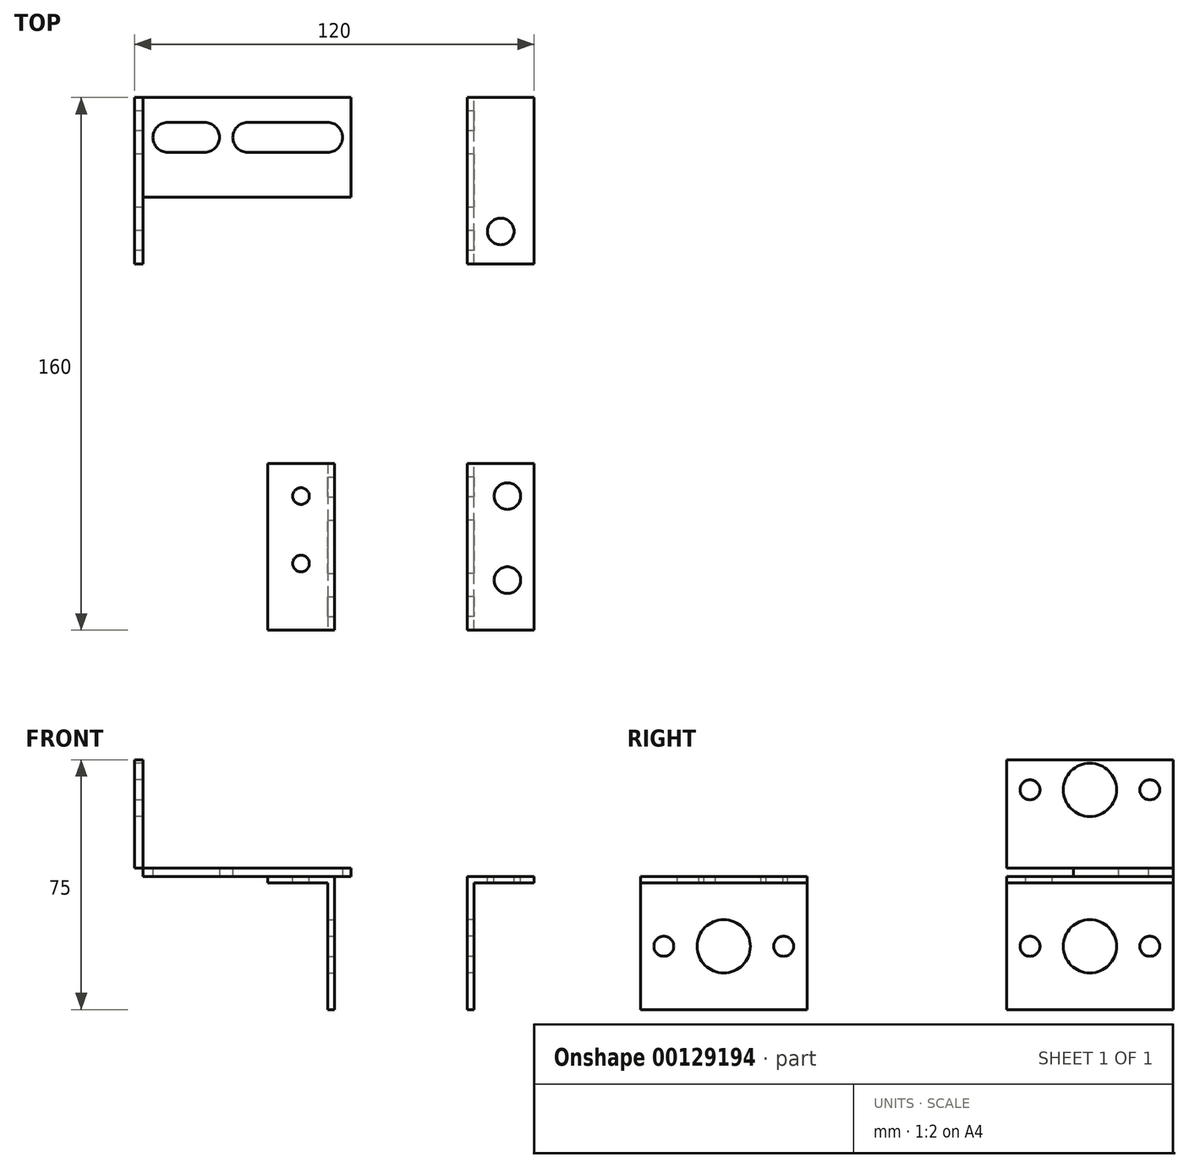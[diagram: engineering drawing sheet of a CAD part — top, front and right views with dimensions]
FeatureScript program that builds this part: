
annotation { "Feature Type Name" : "Feature", "Feature Type Description" : "" }
export const myFeature = defineFeature(function(context is Context, id is Id, definition is map)
    precondition{}
    {
        {
            var Q0;
            Q0=qCreatedBy(makeId("Front.planeOp"),FACE);
            cPlane(context, id + "F0", {"entities" : qUnion([Q0]), "cplaneType" : CPlaneType.OFFSET, "offset" : 80 * mm, "width" : 150 * mm, "height" : 150 * mm});
        }
        {
            var Q0;
            Q0=qCreatedBy(makeId("Front.planeOp"),FACE);
            cPlane(context, id + "F1", {"entities" : qUnion([Q0]), "cplaneType" : CPlaneType.OFFSET, "offset" : 80 * mm, "oppositeDirection" : true, "width" : 150 * mm, "height" : 150 * mm});
        }
        {
            var Q0;
            Q0=qCreatedBy(id+"F0.planeOp",FACE);
            var sketch = newSketch(context, id + "F2", { "sketchPlane" : qUnion([Q0])});
            skLineSegment(sketch, "E0.bottom", {"start": v(-20, 0) * mm, "end": v(-40, 0) * mm});
            skLineSegment(sketch, "E0.top", {"start": v(-20, -2) * mm, "end": v(-40, -2) * mm});
            skLineSegment(sketch, "E0.left", {"start": v(-20, 0) * mm, "end": v(-20, -2) * mm});
            skLineSegment(sketch, "E0.right", {"start": v(-40, 0) * mm, "end": v(-40, -2) * mm});
            skLineSegment(sketch, "E1.bottom", {"start": v(-20, 0) * mm, "end": v(-22, 0) * mm});
            skLineSegment(sketch, "E1.top", {"start": v(-20, -40) * mm, "end": v(-22, -40) * mm});
            skLineSegment(sketch, "E1.left", {"start": v(-20, 0) * mm, "end": v(-20, -40) * mm});
            skLineSegment(sketch, "E1.right", {"start": v(-22, 0) * mm, "end": v(-22, -40) * mm});
            skSolve(sketch);
        }
        {
            var Q0;
            {var subQ0=sQuery(id+"F2.wireOp",EDGE,"E0.bottom");Q0=makeQuery(id+"F2.imprint","IMPRINT",FACE,{"disambiguationData":[TD([[makeQuery(id+"F2.imprint","IMPRINT",EDGE,{"derivedFrom":subQ0}),1.0]])]});}
            var Q1;
            {var subQ5=sQuery(id+"F2.wireOp",EDGE,"E1.bottom");Q1=makeQuery(id+"F2.imprint","IMPRINT",FACE,{"disambiguationData":[TD([[makeQuery(id+"F2.imprint","IMPRINT",EDGE,{"derivedFrom":subQ5}),1.0]])]});}
            extrude(context, id + "F3", {"entities" : qUnion([Q0, Q1]), "oppositeDirection" : true, "depth" : 50 * mm});
        }
        {
            var Q0;
            {var subQ5=sQuery(id+"F2.wireOp",EDGE,"E1.top");Q0=makeQuery(id+"F2.imprint","IMPRINT",FACE,{"disambiguationData":[TD([[makeQuery(id+"F2.imprint","IMPRINT",EDGE,{"derivedFrom":subQ5}),-1.0]])]});}
            var Q1;
            {var subQ5=sQuery(id+"F2.wireOp",EDGE,"E1.bottom");Q1=makeQuery(id+"F2.imprint","IMPRINT",FACE,{"disambiguationData":[TD([[makeQuery(id+"F2.imprint","IMPRINT",EDGE,{"derivedFrom":subQ5}),1.0]])]});}
            extrude(context, id + "F4", {"entities" : qUnion([Q0, Q1]), "operationType" : NewBodyOperationType.ADD, "oppositeDirection" : true, "depth" : 50 * mm});
        }
        {
            var Q0;
            {var subQ0=sQuery(id+"F2.wireOp",EDGE,"E1.left");Q0=makeQuery(id+"F4.boolean.opBoolean","MERGE",FACE,{"derivedFrom":[makeQuery(id+"F3.opExtrude","SWEPT_FACE",FACE,{"disambiguationData":[OSD([subQ0])]}),makeQuery(id+"F4.opExtrude","SWEPT_FACE",FACE,{"disambiguationData":[OSD([subQ0])]})]});}
            var sketch = newSketch(context, id + "F5", { "sketchPlane" : qUnion([Q0])});
            skCircle(sketch, "E2", {"center": v(-55, -21) * mm, "radius": 8 * mm});
            skCircle(sketch, "E3", {"center": v(-73, -21) * mm, "radius": 3 * mm});
            skCircle(sketch, "E4", {"center": v(-37, -21) * mm, "radius": 3 * mm});
            skLineSegment(sketch, "E5", {"start": v(-73, -21) * mm, "end": v(-55, -21) * mm, "construction": true});
            skLineSegment(sketch, "E6", {"start": v(-55, -21) * mm, "end": v(-37, -21) * mm, "construction": true});
            skSolve(sketch);
        }
        {
            var Q0;
            Q0=makeQuery(id+"F3.opExtrude","SWEPT_FACE",FACE,{"disambiguationData":[OSD([sQuery(id+"F2.wireOp",EDGE,"E0.bottom"),sQuery(id+"F2.wireOp",EDGE,"E1.bottom")])]});
            var sketch = newSketch(context, id + "F6", { "sketchPlane" : qUnion([Q0])});
            skCircle(sketch, "E7", {"center": v(-30, -39.75) * mm, "radius": 2.5 * mm});
            skCircle(sketch, "E8", {"center": v(-30, -60) * mm, "radius": 2.5 * mm});
            skSolve(sketch);
        }
        {
            var Q0;
            Q0=makeQuery(id+"F5.imprint","IMPRINT",FACE,{"disambiguationData":[TD([[makeQuery(id+"F5.imprint","IMPRINT",EDGE,{"derivedFrom":sQuery(id+"F5.wireOp",EDGE,"E3")}),1.0]])]});
            var Q1;
            Q1=makeQuery(id+"F5.imprint","IMPRINT",FACE,{"disambiguationData":[TD([[makeQuery(id+"F5.imprint","IMPRINT",EDGE,{"derivedFrom":sQuery(id+"F5.wireOp",EDGE,"E2")}),1.0]])]});
            var Q2;
            Q2=makeQuery(id+"F5.imprint","IMPRINT",FACE,{"disambiguationData":[TD([[makeQuery(id+"F5.imprint","IMPRINT",EDGE,{"derivedFrom":sQuery(id+"F5.wireOp",EDGE,"E4")}),1.0]])]});
            extrude(context, id + "F7", {"entities" : qUnion([Q0, Q1, Q2]), "operationType" : NewBodyOperationType.REMOVE, "endBound" : BoundingType.SYMMETRIC, "oppositeDirection" : true, "depth" : 10 * mm});
        }
        {
            var Q0;
            Q0=makeQuery(id+"F6.imprint","IMPRINT",FACE,{"disambiguationData":[TD([[makeQuery(id+"F6.imprint","IMPRINT",EDGE,{"derivedFrom":sQuery(id+"F6.wireOp",EDGE,"E7")}),1.0]])]});
            var Q1;
            Q1=makeQuery(id+"F6.imprint","IMPRINT",FACE,{"disambiguationData":[TD([[makeQuery(id+"F6.imprint","IMPRINT",EDGE,{"derivedFrom":sQuery(id+"F6.wireOp",EDGE,"E8")}),1.0]])]});
            extrude(context, id + "F8", {"entities" : qUnion([Q0, Q1]), "operationType" : NewBodyOperationType.REMOVE, "endBound" : BoundingType.SYMMETRIC, "oppositeDirection" : true, "depth" : 10 * mm});
        }
        {
            var Q0;
            Q0=qCreatedBy(id+"F0.planeOp",FACE);
            var sketch = newSketch(context, id + "F9", { "sketchPlane" : qUnion([Q0])});
            skLineSegment(sketch, "E9.top", {"start": v(20, -2) * mm, "end": v(40, -2) * mm});
            skLineSegment(sketch, "E9.left", {"start": v(20, 0) * mm, "end": v(20, -2) * mm});
            skLineSegment(sketch, "E9.right", {"start": v(40, 0) * mm, "end": v(40, -2) * mm});
            skLineSegment(sketch, "E10.bottom", {"start": v(20, 0) * mm, "end": v(22, 0) * mm});
            skLineSegment(sketch, "E10.top", {"start": v(20, -40) * mm, "end": v(22, -40) * mm});
            skLineSegment(sketch, "E10.left", {"start": v(20, 0) * mm, "end": v(20, -40) * mm});
            skLineSegment(sketch, "E10.right", {"start": v(22, 0) * mm, "end": v(22, -40) * mm});
            skLineSegment(sketch, "E11", {"start": v(22, 0) * mm, "end": v(40, 0) * mm});
            skSolve(sketch);
        }
        {
            var Q0;
            {var subQ0=sQuery(id+"F9.wireOp",EDGE,"E9.right");Q0=makeQuery(id+"F9.imprint","IMPRINT",FACE,{"disambiguationData":[TD([[makeQuery(id+"F9.imprint","IMPRINT",EDGE,{"derivedFrom":subQ0}),-1.0]])]});}
            var Q1;
            {var subQ5=sQuery(id+"F9.wireOp",EDGE,"E10.bottom");Q1=makeQuery(id+"F9.imprint","IMPRINT",FACE,{"disambiguationData":[TD([[makeQuery(id+"F9.imprint","IMPRINT",EDGE,{"derivedFrom":subQ5}),-1.0]])]});}
            extrude(context, id + "F10", {"entities" : qUnion([Q0, Q1]), "oppositeDirection" : true, "depth" : 50 * mm});
        }
        {
            var Q0;
            {var subQ5=sQuery(id+"F9.wireOp",EDGE,"E10.bottom");Q0=makeQuery(id+"F9.imprint","IMPRINT",FACE,{"disambiguationData":[TD([[makeQuery(id+"F9.imprint","IMPRINT",EDGE,{"derivedFrom":subQ5}),-1.0]])]});}
            var Q1;
            {var subQ5=sQuery(id+"F9.wireOp",EDGE,"E10.top");Q1=makeQuery(id+"F9.imprint","IMPRINT",FACE,{"disambiguationData":[TD([[makeQuery(id+"F9.imprint","IMPRINT",EDGE,{"derivedFrom":subQ5}),1.0]])]});}
            extrude(context, id + "F11", {"entities" : qUnion([Q0, Q1]), "operationType" : NewBodyOperationType.ADD, "oppositeDirection" : true, "depth" : 50 * mm});
        }
        {
            var Q0;
            {var subQ0=sQuery(id+"F9.wireOp",EDGE,"E10.left");Q0=makeQuery(id+"F11.boolean.opBoolean","MERGE",FACE,{"derivedFrom":[makeQuery(id+"F10.opExtrude","SWEPT_FACE",FACE,{"disambiguationData":[OSD([subQ0])]}),makeQuery(id+"F11.opExtrude","SWEPT_FACE",FACE,{"disambiguationData":[OSD([subQ0])]})]});}
            var sketch = newSketch(context, id + "F12", { "sketchPlane" : qUnion([Q0])});
            skCircle(sketch, "E12", {"center": v(55, -21) * mm, "radius": 8 * mm});
            skCircle(sketch, "E13", {"center": v(37, -21) * mm, "radius": 3 * mm});
            skCircle(sketch, "E14", {"center": v(73, -21) * mm, "radius": 3 * mm});
            skLineSegment(sketch, "E15", {"start": v(37, -21) * mm, "end": v(55, -21) * mm, "construction": true});
            skLineSegment(sketch, "E16", {"start": v(55, -21) * mm, "end": v(73, -21) * mm, "construction": true});
            skSolve(sketch);
        }
        {
            var Q0;
            Q0=makeQuery(id+"F10.opExtrude","SWEPT_FACE",FACE,{"disambiguationData":[OSD([sQuery(id+"F9.wireOp",EDGE,"E10.bottom"),sQuery(id+"F9.wireOp",EDGE,"E11")])]});
            var sketch = newSketch(context, id + "F13", { "sketchPlane" : qUnion([Q0])});
            skCircle(sketch, "E17", {"center": v(32, -65) * mm, "radius": 4 * mm});
            skCircle(sketch, "E18", {"center": v(32, -39.75) * mm, "radius": 4 * mm});
            skSolve(sketch);
        }
        {
            var Q0;
            Q0=makeQuery(id+"F12.imprint","IMPRINT",FACE,{"disambiguationData":[TD([[makeQuery(id+"F12.imprint","IMPRINT",EDGE,{"derivedFrom":sQuery(id+"F12.wireOp",EDGE,"E13")}),1.0]])]});
            var Q1;
            Q1=makeQuery(id+"F12.imprint","IMPRINT",FACE,{"disambiguationData":[TD([[makeQuery(id+"F12.imprint","IMPRINT",EDGE,{"derivedFrom":sQuery(id+"F12.wireOp",EDGE,"E12")}),1.0]])]});
            var Q2;
            Q2=makeQuery(id+"F12.imprint","IMPRINT",FACE,{"disambiguationData":[TD([[makeQuery(id+"F12.imprint","IMPRINT",EDGE,{"derivedFrom":sQuery(id+"F12.wireOp",EDGE,"E14")}),1.0]])]});
            extrude(context, id + "F14", {"entities" : qUnion([Q0, Q1, Q2]), "operationType" : NewBodyOperationType.REMOVE, "endBound" : BoundingType.SYMMETRIC, "oppositeDirection" : true, "depth" : 10 * mm});
        }
        {
            var Q0;
            Q0=makeQuery(id+"F13.imprint","IMPRINT",FACE,{"disambiguationData":[TD([[makeQuery(id+"F13.imprint","IMPRINT",EDGE,{"derivedFrom":sQuery(id+"F13.wireOp",EDGE,"E17")}),1.0]])]});
            var Q1;
            Q1=makeQuery(id+"F13.imprint","IMPRINT",FACE,{"disambiguationData":[TD([[makeQuery(id+"F13.imprint","IMPRINT",EDGE,{"derivedFrom":sQuery(id+"F13.wireOp",EDGE,"E18")}),1.0]])]});
            extrude(context, id + "F15", {"entities" : qUnion([Q0, Q1]), "operationType" : NewBodyOperationType.REMOVE, "endBound" : BoundingType.SYMMETRIC, "oppositeDirection" : true, "depth" : 10 * mm});
        }
        {
            var Q0;
            Q0=qCreatedBy(id+"F1.planeOp",FACE);
            var sketch = newSketch(context, id + "F16", { "sketchPlane" : qUnion([Q0])});
            skLineSegment(sketch, "E19", {"start": v(-80, 57.72) * mm, "end": v(-80, -28.34) * mm, "construction": true});
            skLineSegment(sketch, "E20.bottom", {"start": v(-80, 0) * mm, "end": v(-77.5, 0) * mm});
            skLineSegment(sketch, "E20.top", {"start": v(-80, 35) * mm, "end": v(-77.5, 35) * mm});
            skLineSegment(sketch, "E20.left", {"start": v(-80, 0) * mm, "end": v(-80, 35) * mm});
            skLineSegment(sketch, "E20.right", {"start": v(-77.5, 0) * mm, "end": v(-77.5, 35) * mm});
            skLineSegment(sketch, "E21.bottom", {"start": v(-80, 0) * mm, "end": v(-15, 0) * mm});
            skLineSegment(sketch, "E21.top", {"start": v(-80, 2.5) * mm, "end": v(-15, 2.5) * mm});
            skLineSegment(sketch, "E21.left", {"start": v(-80, 0) * mm, "end": v(-80, 2.5) * mm});
            skLineSegment(sketch, "E21.right", {"start": v(-15, 0) * mm, "end": v(-15, 2.5) * mm});
            skSolve(sketch);
        }
        {
            var Q0;
            {var subQ5=sQuery(id+"F16.wireOp",EDGE,"E21.right");Q0=makeQuery(id+"F16.imprint","IMPRINT",FACE,{"disambiguationData":[TD([[makeQuery(id+"F16.imprint","IMPRINT",EDGE,{"derivedFrom":subQ5}),1.0]])]});}
            var Q1;
            {var subQ5=sQuery(id+"F16.wireOp",EDGE,"E21.left");Q1=makeQuery(id+"F16.imprint","IMPRINT",FACE,{"disambiguationData":[TD([[makeQuery(id+"F16.imprint","IMPRINT",EDGE,{"derivedFrom":subQ5}),-1.0]])]});}
            extrude(context, id + "F17", {"entities" : qUnion([Q0, Q1]), "depth" : 30 * mm});
        }
        {
            var Q0;
            {var subQ0=sQuery(id+"F16.wireOp",EDGE,"E20.top");Q0=makeQuery(id+"F16.imprint","IMPRINT",FACE,{"disambiguationData":[TD([[makeQuery(id+"F16.imprint","IMPRINT",EDGE,{"derivedFrom":subQ0}),-1.0]])]});}
            extrude(context, id + "F18", {"entities" : qUnion([Q0]), "operationType" : NewBodyOperationType.ADD, "depth" : 50 * mm});
        }
        {
            var Q0;
            Q0=makeQuery(id+"F18.boolean.opBoolean","MERGE",FACE,{"derivedFrom":[makeQuery(id+"F17.opExtrude","SWEPT_FACE",FACE,{"disambiguationData":[OSD([sQuery(id+"F16.wireOp",EDGE,"E21.left")])]}),makeQuery(id+"F18.opExtrude","SWEPT_FACE",FACE,{"disambiguationData":[OSD([sQuery(id+"F16.wireOp",EDGE,"E20.left")])]})]});
            var sketch = newSketch(context, id + "F19", { "sketchPlane" : qUnion([Q0])});
            skLineSegment(sketch, "E22", {"start": v(-96.06, 26) * mm, "end": v(-5.53, 26) * mm, "construction": true});
            skCircle(sketch, "E23", {"center": v(-55, 26) * mm, "radius": 8 * mm});
            skCircle(sketch, "E24", {"center": v(-73, 26) * mm, "radius": 3 * mm});
            skCircle(sketch, "E25", {"center": v(-37, 26) * mm, "radius": 3 * mm});
            skSolve(sketch);
        }
        {
            var Q0;
            Q0=makeQuery(id+"F17.opExtrude","SWEPT_FACE",FACE,{"disambiguationData":[OSD([sQuery(id+"F16.wireOp",EDGE,"E21.bottom")])]});
            var sketch = newSketch(context, id + "F20", { "sketchPlane" : qUnion([Q0])});
            skLineSegment(sketch, "E26", {"start": v(-92.33, -68) * mm, "end": v(6.09, -68) * mm, "construction": true});
            skArc(sketch, "E27", {"start": v(-70, -63.5) * mm, "mid": v(-74.5, -68) * mm, "end": v(-70, -72.5) * mm});
            skArc(sketch, "E28", {"start": v(-59, -72.5) * mm, "mid": v(-54.5, -68) * mm, "end": v(-59, -63.5) * mm});
            skArc(sketch, "E29", {"start": v(-46, -63.5) * mm, "mid": v(-50.5, -68) * mm, "end": v(-46, -72.5) * mm});
            skArc(sketch, "E30", {"start": v(-22, -72.5) * mm, "mid": v(-17.5, -68) * mm, "end": v(-22, -63.5) * mm});
            skLineSegment(sketch, "E31", {"start": v(-70, -63.5) * mm, "end": v(-59, -63.5) * mm});
            skLineSegment(sketch, "E32", {"start": v(-70, -72.5) * mm, "end": v(-59, -72.5) * mm});
            skLineSegment(sketch, "E33", {"start": v(-46, -72.5) * mm, "end": v(-22, -72.5) * mm});
            skLineSegment(sketch, "E34", {"start": v(-46, -63.5) * mm, "end": v(-22, -63.5) * mm});
            skSolve(sketch);
        }
        {
            var Q0;
            Q0=makeQuery(id+"F19.imprint","IMPRINT",FACE,{"disambiguationData":[TD([[makeQuery(id+"F19.imprint","IMPRINT",EDGE,{"derivedFrom":sQuery(id+"F19.wireOp",EDGE,"E24")}),1.0]])]});
            var Q1;
            Q1=makeQuery(id+"F19.imprint","IMPRINT",FACE,{"disambiguationData":[TD([[makeQuery(id+"F19.imprint","IMPRINT",EDGE,{"derivedFrom":sQuery(id+"F19.wireOp",EDGE,"E23")}),1.0]])]});
            var Q2;
            Q2=makeQuery(id+"F19.imprint","IMPRINT",FACE,{"disambiguationData":[TD([[makeQuery(id+"F19.imprint","IMPRINT",EDGE,{"derivedFrom":sQuery(id+"F19.wireOp",EDGE,"E25")}),1.0]])]});
            extrude(context, id + "F21", {"entities" : qUnion([Q0, Q1, Q2]), "operationType" : NewBodyOperationType.REMOVE, "endBound" : BoundingType.SYMMETRIC, "oppositeDirection" : true, "depth" : 10 * mm});
        }
        {
            var Q0;
            Q0=makeQuery(id+"F20.imprint","IMPRINT",FACE,{"disambiguationData":[TD([[makeQuery(id+"F20.imprint","IMPRINT",EDGE,{"derivedFrom":sQuery(id+"F20.wireOp",EDGE,"E27")}),1.0]])]});
            var Q1;
            Q1=makeQuery(id+"F20.imprint","IMPRINT",FACE,{"disambiguationData":[TD([[makeQuery(id+"F20.imprint","IMPRINT",EDGE,{"derivedFrom":sQuery(id+"F20.wireOp",EDGE,"E29")}),1.0]])]});
            extrude(context, id + "F22", {"entities" : qUnion([Q0, Q1]), "operationType" : NewBodyOperationType.REMOVE, "endBound" : BoundingType.SYMMETRIC, "oppositeDirection" : true, "depth" : 10 * mm});
        }
        {
            var Q0;
            Q0=qCreatedBy(id+"F1.planeOp",FACE);
            var sketch = newSketch(context, id + "F23", { "sketchPlane" : qUnion([Q0])});
            skLineSegment(sketch, "E35.bottom", {"start": v(40, 0) * mm, "end": v(20, 0) * mm});
            skLineSegment(sketch, "E35.top", {"start": v(40, -2) * mm, "end": v(20, -2) * mm});
            skLineSegment(sketch, "E35.left", {"start": v(40, 0) * mm, "end": v(40, -2) * mm});
            skLineSegment(sketch, "E35.right", {"start": v(20, 0) * mm, "end": v(20, -2) * mm});
            skLineSegment(sketch, "E36.bottom", {"start": v(20, 0) * mm, "end": v(22, 0) * mm});
            skLineSegment(sketch, "E36.top", {"start": v(20, -40) * mm, "end": v(22, -40) * mm});
            skLineSegment(sketch, "E36.left", {"start": v(20, 0) * mm, "end": v(20, -40) * mm});
            skLineSegment(sketch, "E36.right", {"start": v(22, 0) * mm, "end": v(22, -40) * mm});
            skSolve(sketch);
        }
        {
            var Q0;
            {var subQ0=sQuery(id+"F23.wireOp",EDGE,"E35.bottom");Q0=makeQuery(id+"F23.imprint","IMPRINT",FACE,{"disambiguationData":[TD([[makeQuery(id+"F23.imprint","IMPRINT",EDGE,{"derivedFrom":subQ0}),1.0]])]});}
            var Q1;
            {var subQ5=sQuery(id+"F23.wireOp",EDGE,"E36.bottom");Q1=makeQuery(id+"F23.imprint","IMPRINT",FACE,{"disambiguationData":[TD([[makeQuery(id+"F23.imprint","IMPRINT",EDGE,{"derivedFrom":subQ5}),-1.0]])]});}
            extrude(context, id + "F24", {"entities" : qUnion([Q0, Q1]), "depth" : 50 * mm});
        }
        {
            var Q0;
            {var subQ5=sQuery(id+"F23.wireOp",EDGE,"E36.top");Q0=makeQuery(id+"F23.imprint","IMPRINT",FACE,{"disambiguationData":[TD([[makeQuery(id+"F23.imprint","IMPRINT",EDGE,{"derivedFrom":subQ5}),1.0]])]});}
            var Q1;
            {var subQ5=sQuery(id+"F23.wireOp",EDGE,"E36.bottom");Q1=makeQuery(id+"F23.imprint","IMPRINT",FACE,{"disambiguationData":[TD([[makeQuery(id+"F23.imprint","IMPRINT",EDGE,{"derivedFrom":subQ5}),-1.0]])]});}
            extrude(context, id + "F25", {"entities" : qUnion([Q0, Q1]), "operationType" : NewBodyOperationType.ADD, "depth" : 50 * mm});
        }
        {
            var Q0;
            {var subQ0=sQuery(id+"F23.wireOp",EDGE,"E36.left");Q0=makeQuery(id+"F25.boolean.opBoolean","MERGE",FACE,{"derivedFrom":[makeQuery(id+"F24.opExtrude","SWEPT_FACE",FACE,{"disambiguationData":[OSD([subQ0])]}),makeQuery(id+"F25.opExtrude","SWEPT_FACE",FACE,{"disambiguationData":[OSD([subQ0])]})]});}
            var sketch = newSketch(context, id + "F26", { "sketchPlane" : qUnion([Q0])});
            skLineSegment(sketch, "E37", {"start": v(-95.84, -21) * mm, "end": v(-16.28, -21) * mm, "construction": true});
            skCircle(sketch, "E38", {"center": v(-55, -21) * mm, "radius": 8 * mm});
            skCircle(sketch, "E39", {"center": v(-73, -21) * mm, "radius": 3 * mm});
            skCircle(sketch, "E40", {"center": v(-37, -21) * mm, "radius": 3 * mm});
            skSolve(sketch);
        }
        {
            var Q0;
            Q0=makeQuery(id+"F24.opExtrude","SWEPT_FACE",FACE,{"disambiguationData":[OSD([sQuery(id+"F23.wireOp",EDGE,"E35.bottom"),sQuery(id+"F23.wireOp",EDGE,"E36.bottom")])]});
            var sketch = newSketch(context, id + "F27", { "sketchPlane" : qUnion([Q0])});
            skCircle(sketch, "E41", {"center": v(30, 39.75) * mm, "radius": 4 * mm});
            skSolve(sketch);
        }
        {
            var Q0;
            Q0=makeQuery(id+"F26.imprint","IMPRINT",FACE,{"disambiguationData":[TD([[makeQuery(id+"F26.imprint","IMPRINT",EDGE,{"derivedFrom":sQuery(id+"F26.wireOp",EDGE,"E39")}),1.0]])]});
            var Q1;
            Q1=makeQuery(id+"F26.imprint","IMPRINT",FACE,{"disambiguationData":[TD([[makeQuery(id+"F26.imprint","IMPRINT",EDGE,{"derivedFrom":sQuery(id+"F26.wireOp",EDGE,"E38")}),1.0]])]});
            var Q2;
            Q2=makeQuery(id+"F26.imprint","IMPRINT",FACE,{"disambiguationData":[TD([[makeQuery(id+"F26.imprint","IMPRINT",EDGE,{"derivedFrom":sQuery(id+"F26.wireOp",EDGE,"E40")}),1.0]])]});
            extrude(context, id + "F28", {"entities" : qUnion([Q0, Q1, Q2]), "operationType" : NewBodyOperationType.REMOVE, "endBound" : BoundingType.SYMMETRIC, "oppositeDirection" : true, "depth" : 10 * mm});
        }
        {
            var Q0;
            Q0=makeQuery(id+"F27.imprint","IMPRINT",FACE,{"disambiguationData":[TD([[makeQuery(id+"F27.imprint","IMPRINT",EDGE,{"derivedFrom":sQuery(id+"F27.wireOp",EDGE,"E41")}),1.0]])]});
            extrude(context, id + "F29", {"entities" : qUnion([Q0]), "operationType" : NewBodyOperationType.REMOVE, "endBound" : BoundingType.SYMMETRIC, "oppositeDirection" : true, "depth" : 10 * mm});
        }
    });
